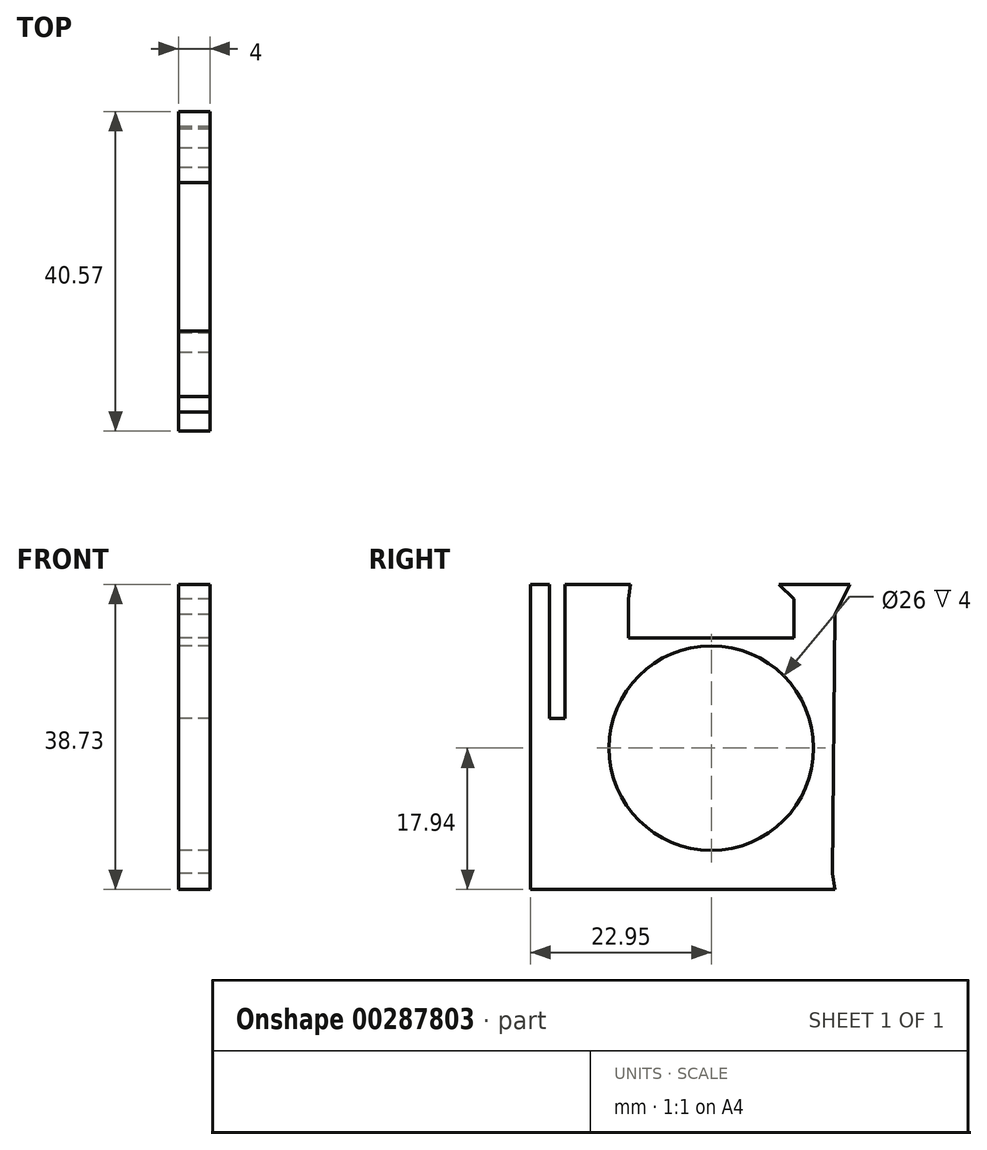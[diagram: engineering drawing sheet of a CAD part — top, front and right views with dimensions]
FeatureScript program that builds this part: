
annotation { "Feature Type Name" : "Feature", "Feature Type Description" : "" }
export const myFeature = defineFeature(function(context is Context, id is Id, definition is map)
    precondition{}
    {
        {
            var Q0;
            Q0=qCreatedBy(makeId("Right.planeOp"),FACE);
            var sketch = newSketch(context, id + "F0", { "sketchPlane" : qUnion([Q0])});
            skCircle(sketch, "E0", {"center": v(0, 0) * mm, "radius": 13 * mm});
            skLineSegment(sketch, "E1.top", {"start": v(-22.95, -15.94) * mm, "end": v(22.95, -15.94) * mm});
            skLineSegment(sketch, "E1.left", {"start": v(-22.95, 20.8) * mm, "end": v(-22.95, -15.94) * mm});
            skLineSegment(sketch, "E1.right", {"start": v(22.95, 20.8) * mm, "end": v(22.95, -15.94) * mm});
            skLineSegment(sketch, "E2", {"start": v(0, 20.8) * mm, "end": v(0, -15.94) * mm, "construction": true});
            skLineSegment(sketch, "E3.top", {"start": v(10.5, 13.97) * mm, "end": v(-10.5, 13.97) * mm});
            skLineSegment(sketch, "E3.left", {"start": v(10.5, 18.97) * mm, "end": v(10.5, 13.97) * mm});
            skLineSegment(sketch, "E3.right", {"start": v(-10.5, 18.97) * mm, "end": v(-10.5, 13.97) * mm});
            skPoint(sketch, "E3.middle", {"position": v(0, 16.47) * mm});
            skLineSegment(sketch, "E4.MirrorCS", {"start": v(-10.5, 18.97) * mm, "end": v(-10.25, 20.8) * mm});
            skLineSegment(sketch, "E5.bottom", {"start": v(-20.57, 20.8) * mm, "end": v(-18.57, 20.8) * mm, "construction": true});
            skLineSegment(sketch, "E5.top", {"start": v(-20.57, 3.8) * mm, "end": v(-18.57, 3.8) * mm});
            skLineSegment(sketch, "E5.left", {"start": v(-20.57, 20.8) * mm, "end": v(-20.57, 3.8) * mm});
            skLineSegment(sketch, "E5.right", {"start": v(-18.57, 20.8) * mm, "end": v(-18.57, 3.8) * mm});
            skLineSegment(sketch, "E6", {"start": v(15.68, 17) * mm, "end": v(17.62, 20.8) * mm});
            skLineSegment(sketch, "E7", {"start": v(15.41, -15.94) * mm, "end": v(15.68, 17) * mm});
            skLineSegment(sketch, "E8.top", {"start": v(-22.95, -17.94) * mm, "end": v(22.95, -17.94) * mm});
            skLineSegment(sketch, "E8.left", {"start": v(-22.95, -15.94) * mm, "end": v(-22.95, -17.94) * mm});
            skLineSegment(sketch, "E8.right", {"start": v(22.95, -15.94) * mm, "end": v(22.95, -17.94) * mm});
            skLineSegment(sketch, "E9.top", {"start": v(10.5, 20.8) * mm, "end": v(8.58, 20.8) * mm});
            skLineSegment(sketch, "E10", {"start": v(8.58, 20.8) * mm, "end": v(10.5, 18.97) * mm});
            skLineSegment(sketch, "E11", {"start": v(-22.95, 20.8) * mm, "end": v(-20.57, 20.8) * mm});
            skLineSegment(sketch, "E12", {"start": v(-18.57, 20.8) * mm, "end": v(-10.25, 20.8) * mm});
            skLineSegment(sketch, "E13", {"start": v(10.5, 20.8) * mm, "end": v(22.95, 20.8) * mm});
            skLineSegment(sketch, "E14", {"start": v(15.41, -15.94) * mm, "end": v(15.7, -17.94) * mm});
            skSolve(sketch);
        }
        {
            var Q0;
            {var subQ0=sQuery(id+"F0.wireOp",EDGE,"E8.left");Q0=makeQuery(id+"F0.imprint","IMPRINT",FACE,{"disambiguationData":[TD([[makeQuery(id+"F0.imprint","IMPRINT",EDGE,{"derivedFrom":subQ0}),1.0]])]});}
            var Q1;
            Q1=makeQuery(id+"F0.imprint","IMPRINT",FACE,{"disambiguationData":[TD([[makeQuery(id+"F0.imprint","IMPRINT",EDGE,{"derivedFrom":sQuery(id+"F0.wireOp",EDGE,"E0")}),-1.0]])]});
            extrude(context, id + "F1", {"entities" : qUnion([Q0, Q1]), "depth" : 4 * mm, "offsetDistance" : 25 * mm});
        }
    });
